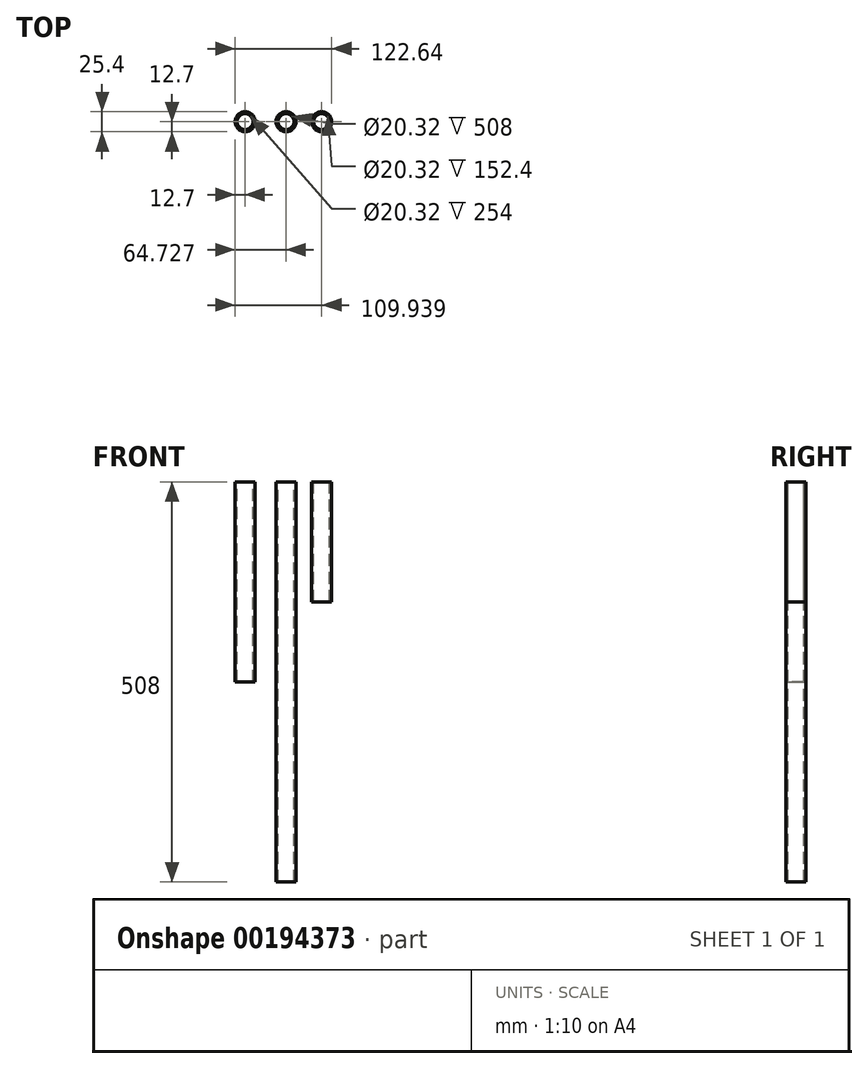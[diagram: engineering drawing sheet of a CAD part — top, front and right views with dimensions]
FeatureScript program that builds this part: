
annotation { "Feature Type Name" : "Feature", "Feature Type Description" : "" }
export const myFeature = defineFeature(function(context is Context, id is Id, definition is map)
    precondition{}
    {
        {
            var Q0;
            Q0=qCreatedBy(makeId("Front.planeOp"),FACE);
            var sketch = newSketch(context, id + "F0", { "sketchPlane" : qUnion([Q0])});
            skLineSegment(sketch, "E0", {"start": v(0, 58.7) * mm, "end": v(0, -194) * mm, "construction": true});
            skLineSegment(sketch, "E1.bottom", {"start": v(10.16, 0) * mm, "end": v(12.7, 0) * mm});
            skLineSegment(sketch, "E1.top", {"start": v(10.16, -254) * mm, "end": v(12.7, -254) * mm});
            skLineSegment(sketch, "E1.left", {"start": v(10.16, 0) * mm, "end": v(10.16, -254) * mm});
            skLineSegment(sketch, "E1.right", {"start": v(12.7, 0) * mm, "end": v(12.7, -254) * mm});
            skSolve(sketch);
        }
        {
            var Q0;
            Q0=qSketchRegion(id+"F0",true);
            var Q1;
            Q1=sQuery(id+"F0.wireOp",EDGE,"E0");
            revolve(context, id + "F1", {"entities" : qUnion([Q0]), "axis" : qUnion([Q1]), "revolveType" : RevolveType.FULL});
        }
        {
            var Q0;
            Q0=qCreatedBy(makeId("Top.planeOp"),FACE);
            var sketch = newSketch(context, id + "F2", { "sketchPlane" : qUnion([Q0])});
            skCircle(sketch, "E2", {"center": v(52.03, 0) * mm, "radius": 12.7 * mm});
            skCircle(sketch, "E3", {"center": v(52.03, 0) * mm, "radius": 10.16 * mm});
            skCircle(sketch, "E4.1.0.0", {"center": v(97.24, 0) * mm, "radius": 12.7 * mm});
            skCircle(sketch, "E4.1.0.1", {"center": v(97.24, 0) * mm, "radius": 10.16 * mm});
            skCircle(sketch, "E4.2.0.0", {"center": v(142.45, 0) * mm, "radius": 12.7 * mm});
            skCircle(sketch, "E4.2.0.1", {"center": v(142.45, 0) * mm, "radius": 10.16 * mm});
            skLineSegment(sketch, "E4.direction1", {"start": v(52.03, 0) * mm, "end": v(97.24, 0) * mm, "construction": true});
            skSolve(sketch);
        }
        {
            var Q0;
            Q0=makeQuery(id+"F2.imprint","IMPRINT",FACE,{"disambiguationData":[TD([[makeQuery(id+"F2.imprint","IMPRINT",EDGE,{"derivedFrom":sQuery(id+"F2.wireOp",EDGE,"E2")}),1.0]])]});
            extrude(context, id + "F3", {"entities" : qUnion([Q0]), "oppositeDirection" : true, "depth" : 508 * mm});
        }
        {
            var Q0;
            Q0=makeQuery(id+"F2.imprint","IMPRINT",FACE,{"disambiguationData":[TD([[makeQuery(id+"F2.imprint","IMPRINT",EDGE,{"derivedFrom":sQuery(id+"F2.wireOp",EDGE,"E4.1.0.0")}),1.0]])]});
            extrude(context, id + "F4", {"entities" : qUnion([Q0]), "oppositeDirection" : true, "depth" : 152.4 * mm});
        }
    });
